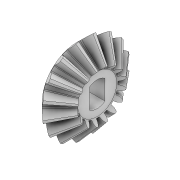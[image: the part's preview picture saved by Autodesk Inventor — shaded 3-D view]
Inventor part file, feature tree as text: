
AUTODESK INVENTOR PART (.ipt)
format: ipt  version: 2020 (Build 240168000, 168)  size: 875,520 bytes
history: native  units: in
note: dims shown in document units (in); Inventor stores cm internally (conversion verified against a paired STEP export)
features: other x3, extrude x2, sketch x2, projected_geometry x1
ambient origin geometry x8: Origin, YZ Plane, XZ Plane, XY Plane, X Axis, Y Axis, Z Axis, Center Point
bodies: Solid1 (feature_tree)
feature tree (8):
  other  "straight_miter_gear_isoiso_-_st.ipt"
  extrude  "Extrusion1"  Depth=0.122in
  extrude  "Extrusion2"  Depth=1.0in TaperAngle=0.0deg
  other  "Solid1::straight_miter_gear_isoiso_-_st.ipt"
  other  "TaggingFeature1"
  sketch  "Sketch1"  dims[d0=0.0394in d1=0.122in]
  sketch  "Sketch2"  dims[d2=0.061in d3=1.0in d4=0.0in d5=1.0in d6=0.0in]
  projected_geometry  "Projected Loop1"
